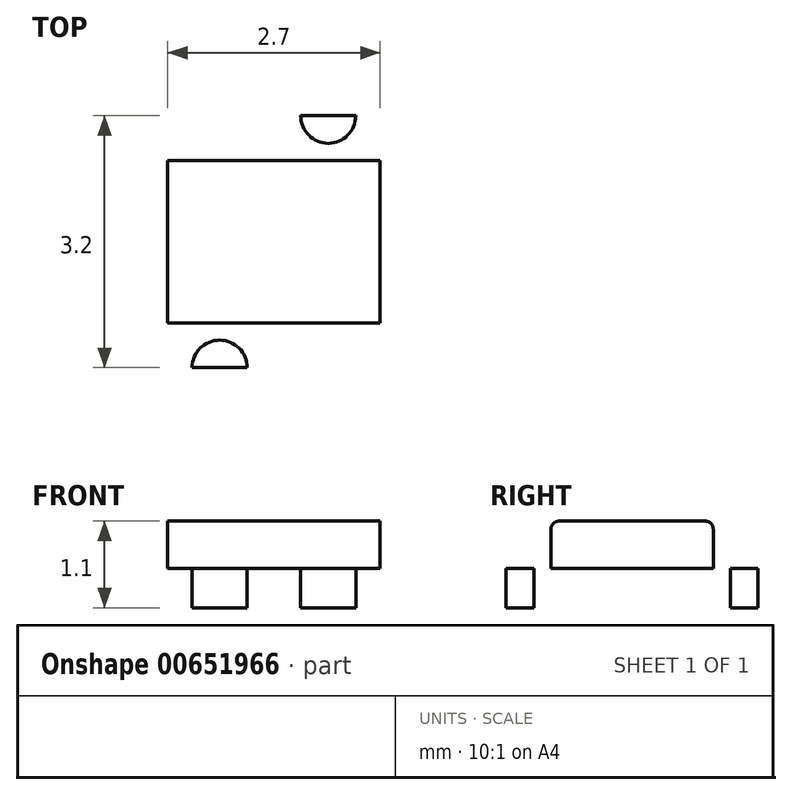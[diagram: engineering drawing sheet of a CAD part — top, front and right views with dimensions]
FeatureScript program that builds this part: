
annotation { "Feature Type Name" : "Feature", "Feature Type Description" : "" }
export const myFeature = defineFeature(function(context is Context, id is Id, definition is map)
    precondition{}
    {
        {
            var Q0;
            Q0=qCreatedBy(makeId("Top.planeOp"),FACE);
            var sketch = newSketch(context, id + "F0", { "sketchPlane" : qUnion([Q0])});
            skLineSegment(sketch, "E0.bottom", {"start": v(1.35, -1.6) * mm, "end": v(-1.35, -1.6) * mm});
            skLineSegment(sketch, "E0.top", {"start": v(1.35, 1.6) * mm, "end": v(-1.35, 1.6) * mm});
            skLineSegment(sketch, "E0.left", {"start": v(1.35, -1.6) * mm, "end": v(1.35, 1.6) * mm});
            skLineSegment(sketch, "E0.right", {"start": v(-1.35, -1.6) * mm, "end": v(-1.35, 1.6) * mm});
            skPoint(sketch, "E0.middle", {"position": v(0, 0) * mm});
            skSolve(sketch);
        }
        {
            var Q0;
            Q0=makeQuery(id+"F0.imprint","IMPRINT",FACE,{"disambiguationData":[TD([[makeQuery(id+"F0.imprint","IMPRINT",EDGE,{"derivedFrom":sQuery(id+"F0.wireOp",EDGE,"E0.bottom")}),-1.0]])]});
            extrude(context, id + "F1", {"entities" : qUnion([Q0]), "depth" : .5 * mm, "offsetDistance" : 25 * mm});
        }
        {
            var Q0;
            Q0=makeQuery(id+"F1.opExtrude","CAP_FACE",FACE,{"disambiguationData":[OSD([sQuery(id+"F0.wireOp",EDGE,"E0.bottom"),sQuery(id+"F0.wireOp",EDGE,"E0.top"),sQuery(id+"F0.wireOp",EDGE,"E0.left"),sQuery(id+"F0.wireOp",EDGE,"E0.right")])],"isStart":false});
            var sketch = newSketch(context, id + "F2", { "sketchPlane" : qUnion([Q0])});
            skPoint(sketch, "E1", {"position": v(-0.69, 1.6) * mm});
            skArc(sketch, "E2", {"start": v(-1.04, 1.6) * mm, "mid": v(-0.69, 1.25) * mm, "end": v(-0.34, 1.6) * mm});
            skLineSegment(sketch, "E3", {"start": v(-1.04, 1.6) * mm, "end": v(-0.34, 1.6) * mm});
            skArc(sketch, "E4.MirrorCS", {"start": v(1.04, 1.6) * mm, "mid": v(0.69, 1.25) * mm, "end": v(0.34, 1.6) * mm});
            skLineSegment(sketch, "E5.MirrorCS", {"start": v(1.04, 1.6) * mm, "end": v(0.34, 1.6) * mm});
            skArc(sketch, "E6.MirrorCS", {"start": v(-1.04, -1.6) * mm, "mid": v(-0.69, -1.25) * mm, "end": v(-0.34, -1.6) * mm});
            skLineSegment(sketch, "E7.MirrorCS", {"start": v(-1.04, -1.6) * mm, "end": v(-0.34, -1.6) * mm});
            skArc(sketch, "E8.MirrorCS", {"start": v(1.04, -1.6) * mm, "mid": v(0.69, -1.25) * mm, "end": v(0.34, -1.6) * mm});
            skLineSegment(sketch, "E9.MirrorCS", {"start": v(1.04, -1.6) * mm, "end": v(0.34, -1.6) * mm});
            skSolve(sketch);
        }
        {
            var Q0;
            Q0=makeQuery(id+"F2.imprint","IMPRINT",FACE,{"disambiguationData":[TD([[makeQuery(id+"F2.imprint","IMPRINT",EDGE,{"derivedFrom":sQuery(id+"F2.wireOp",EDGE,"E2")}),1.0]])]});
            var Q1;
            Q1=makeQuery(id+"F2.imprint","IMPRINT",FACE,{"disambiguationData":[TD([[makeQuery(id+"F2.imprint","IMPRINT",EDGE,{"derivedFrom":sQuery(id+"F2.wireOp",EDGE,"E4.MirrorCS")}),-1.0]])]});
            var Q2;
            Q2=makeQuery(id+"F2.imprint","IMPRINT",FACE,{"disambiguationData":[TD([[makeQuery(id+"F2.imprint","IMPRINT",EDGE,{"derivedFrom":sQuery(id+"F2.wireOp",EDGE,"E8.MirrorCS")}),1.0]])]});
            var Q3;
            Q3=makeQuery(id+"F2.imprint","IMPRINT",FACE,{"disambiguationData":[TD([[makeQuery(id+"F2.imprint","IMPRINT",EDGE,{"derivedFrom":sQuery(id+"F2.wireOp",EDGE,"E6.MirrorCS")}),-1.0]])]});
            extrude(context, id + "F3", {"entities" : qUnion([Q0, Q1, Q2, Q3]), "operationType" : NewBodyOperationType.REMOVE, "endBound" : BoundingType.THROUGH_ALL, "oppositeDirection" : true, "depth" : 25 * mm, "offsetDistance" : 25 * mm});
        }
        {
            var Q0;
            Q0=makeQuery(id+"F1.opExtrude","CAP_FACE",FACE,{"disambiguationData":[OSD([sQuery(id+"F0.wireOp",EDGE,"E0.bottom"),sQuery(id+"F0.wireOp",EDGE,"E0.top"),sQuery(id+"F0.wireOp",EDGE,"E0.left"),sQuery(id+"F0.wireOp",EDGE,"E0.right")])],"isStart":false});
            var sketch = newSketch(context, id + "F4", { "sketchPlane" : qUnion([Q0])});
            skLineSegment(sketch, "E10.bottom", {"start": v(1.35, -1.03) * mm, "end": v(-1.35, -1.03) * mm});
            skLineSegment(sketch, "E10.top", {"start": v(1.35, 1.03) * mm, "end": v(-1.35, 1.03) * mm});
            skLineSegment(sketch, "E10.left", {"start": v(1.35, -1.03) * mm, "end": v(1.35, 1.03) * mm});
            skLineSegment(sketch, "E10.right", {"start": v(-1.35, -1.03) * mm, "end": v(-1.35, 1.03) * mm});
            skPoint(sketch, "E10.middle", {"position": v(0, 0) * mm});
            skSolve(sketch);
        }
        {
            var Q0;
            Q0 = qSketchRegion(id + "F4", true);
            extrude(context, id + "F5", {"entities" : qUnion([Q0]), "operationType" : NewBodyOperationType.ADD, "depth" : .6 * mm, "offsetDistance" : 25 * mm});
        }
        {
            var Q0;
            Q0=makeQuery(id+"F5.opExtrude","CAP_EDGE",EDGE,{"disambiguationData":[OSD([sQuery(id+"F4.wireOp",EDGE,"E10.top")])],"isStart":false});
            var Q1;
            Q1=makeQuery(id+"F5.opExtrude","CAP_EDGE",EDGE,{"disambiguationData":[OSD([sQuery(id+"F4.wireOp",EDGE,"E10.bottom")])],"isStart":false});
            fillet(context, id + "F6", {"entities" : qUnion([Q0, Q1]), "radius" : .1 * mm, "tangentPropagation" : true, "allowEdgeOverflow" : false});
        }
    });
